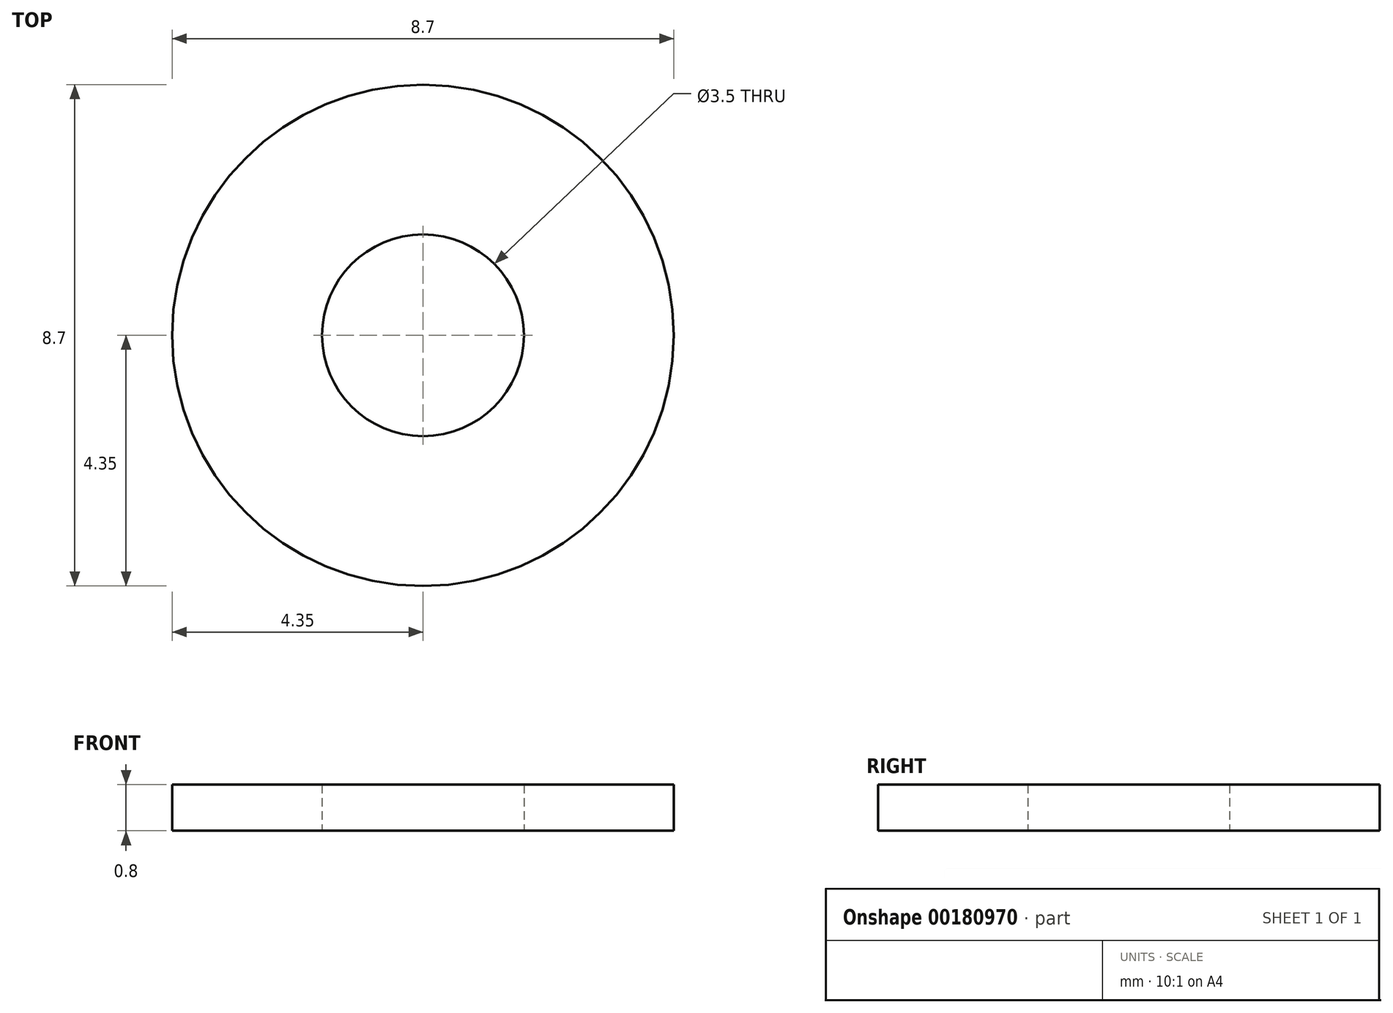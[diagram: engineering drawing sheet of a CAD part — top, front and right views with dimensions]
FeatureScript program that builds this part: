
annotation { "Feature Type Name" : "Feature", "Feature Type Description" : "" }
export const myFeature = defineFeature(function(context is Context, id is Id, definition is map)
    precondition{}
    {
        {
            var Q0;
            Q0=qCreatedBy(makeId("Top.planeOp"),FACE);
            var sketch = newSketch(context, id + "F0", { "sketchPlane" : qUnion([Q0])});
            skCircle(sketch, "E0", {"center": v(0, 0) * mm, "radius": 4.35 * mm});
            skCircle(sketch, "E1", {"center": v(0, 0) * mm, "radius": 1.75 * mm});
            skSolve(sketch);
        }
        {
            var Q0;
            Q0=qSketchRegion(id+"F0",true);
            extrude(context, id + "F1", {"entities" : qUnion([Q0]), "depth" : 0.8 * mm});
        }
    });
